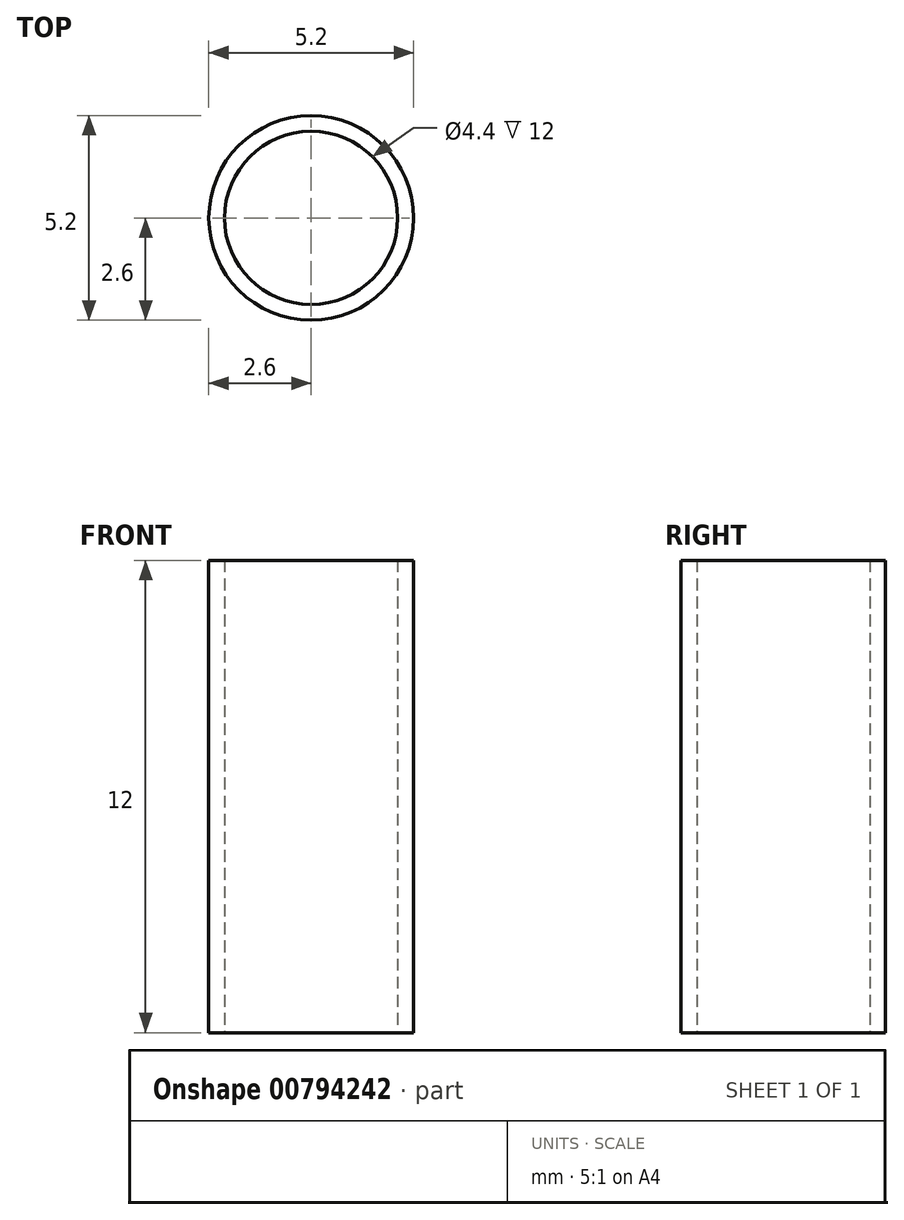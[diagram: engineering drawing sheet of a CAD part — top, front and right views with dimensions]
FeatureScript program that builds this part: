
annotation { "Feature Type Name" : "Feature", "Feature Type Description" : "" }
export const myFeature = defineFeature(function(context is Context, id is Id, definition is map)
    precondition{}
    {
        {
            var Q0;
            Q0=qCreatedBy(makeId("Top.planeOp"),FACE);
            var sketch = newSketch(context, id + "F0", { "sketchPlane" : qUnion([Q0])});
            skCircle(sketch, "E0", {"center": v(0, 0) * mm, "radius": 2.6 * mm});
            skCircle(sketch, "E1", {"center": v(0, 0) * mm, "radius": 2.2 * mm});
            skSolve(sketch);
        }
        {
            var Q0;
            Q0=makeQuery(id+"F0.imprint","IMPRINT",FACE,{"disambiguationData":[TD([[makeQuery(id+"F0.imprint","IMPRINT",EDGE,{"derivedFrom":sQuery(id+"F0.wireOp",EDGE,"E0")}),1.0]])]});
            extrude(context, id + "F1", {"entities" : qUnion([Q0]), "depth" : 12 * mm, "offsetDistance" : 25 * mm});
        }
    });
